# Revit family: CBCGTYP007
name_source: partatom
category: Furniture
units: mm (PartAtom-declared; Revit-internal decimal feet)

## family parameters
Always vertical = Yes
Cut with Voids When Loaded = No
OmniClass Number = 23.40.20.00
OmniClass Title = General Furniture and Specialties
Render Appearance Source = Family Geometry
Room Calculation Point = No
Shared = No
Work Plane-Based = No

## types (1)
- CBCGTYP007
    Cost = 22276 $
    Default Elevation = 0 mm  [stored 0 ft]
    Description = 1 x CBX Full Depth Floor Bookcase 24Dx21Hx36W, 2 x Cb Wall Mounted Cabinet Double Height 14dx32hx36w, 1 x Cb Wall Mounted Bookcase Double Height 14dx32hx36w, 2 x Cbx Full Depth Lat Bf 24dx21hx36w, 1 x CBX O-LEG Stack-On Desk 28"h X 72"w X 30"d, 1 x Cbx Tackboard Wall Mount 28hx36w, 1 x Cbx Tackboard Wall Mount 28hx72w, 1 x Cbx Open Front Bf Wardrobe Rh 24dx82hx24w
    Exported From CET Designer = Yes
    Manufacturer = AIS
    Model = X-CBC203624
    Show CBCGTYP007 = Yes
    VisibilityIndex = 0

note: [stored X ft] marks values corroborated as IEEE doubles in the binary element streams (Revit-internal decimal feet)

## geometry (parser evidence)
native form markers: Sweep x3
no freeform markers — native parametric forms only
